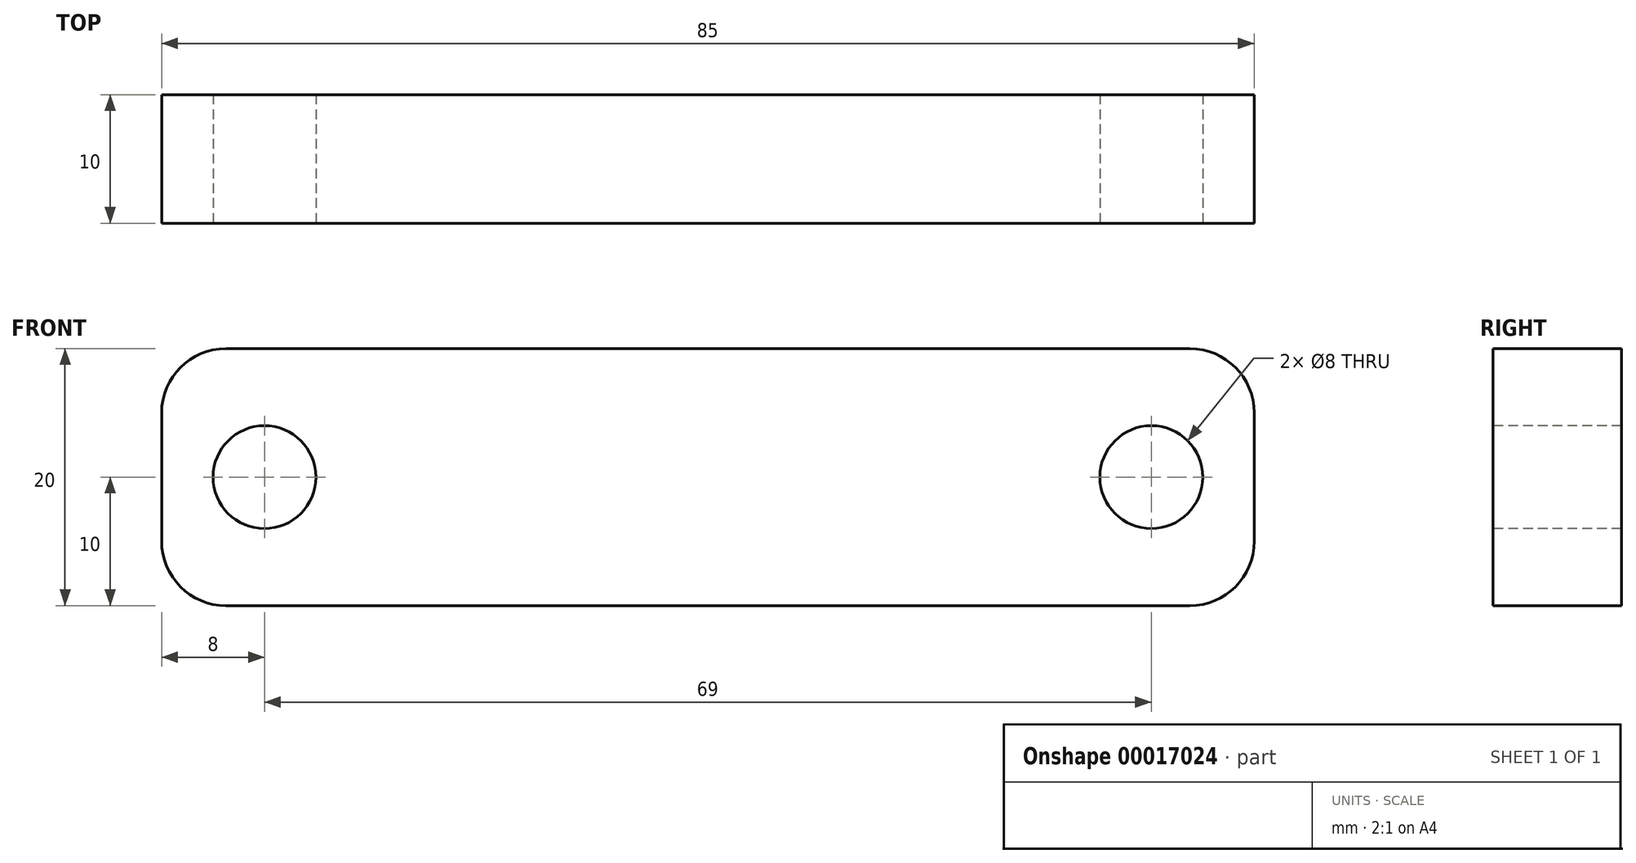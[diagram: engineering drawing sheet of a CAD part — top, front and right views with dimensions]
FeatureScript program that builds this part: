
annotation { "Feature Type Name" : "Feature", "Feature Type Description" : "" }
export const myFeature = defineFeature(function(context is Context, id is Id, definition is map)
    precondition{}
    {
        {
            var Q0;
            Q0=qCreatedBy(makeId("Front.planeOp"),FACE);
            var sketch = newSketch(context, id + "F0", { "sketchPlane" : qUnion([Q0])});
            skLineSegment(sketch, "E0.bottom", {"start": v(-40, 10) * mm, "end": v(45, 10) * mm});
            skLineSegment(sketch, "E0.top", {"start": v(-40, -10) * mm, "end": v(45, -10) * mm});
            skLineSegment(sketch, "E0.left", {"start": v(-40, 10) * mm, "end": v(-40, -10) * mm});
            skLineSegment(sketch, "E0.right", {"start": v(45, 10) * mm, "end": v(45, -10) * mm});
            skSolve(sketch);
        }
        {
            var Q0;
            Q0 = qSketchRegion(id + "F0", true);
            extrude(context, id + "F1", {"entities" : qUnion([Q0]), "depth" : 10 * mm});
        }
        {
            var Q0;
            Q0=makeQuery(id+"F1.opExtrude","CAP_FACE",FACE,{"disambiguationData":[OSD([sQuery(id+"F0.wireOp",EDGE,"E0.bottom"),sQuery(id+"F0.wireOp",EDGE,"E0.top"),sQuery(id+"F0.wireOp",EDGE,"E0.left"),sQuery(id+"F0.wireOp",EDGE,"E0.right")])],"isStart":false});
            var sketch = newSketch(context, id + "F2", { "sketchPlane" : qUnion([Q0])});
            skCircle(sketch, "E1", {"center": v(37, 0) * mm, "radius": 4 * mm});
            skCircle(sketch, "E2", {"center": v(-32, 0) * mm, "radius": 4 * mm});
            skSolve(sketch);
        }
        {
            var Q0;
            Q0 = qSketchRegion(id + "F2", true);
            extrude(context, id + "F3", {"entities" : qUnion([Q0]), "operationType" : NewBodyOperationType.REMOVE, "endBound" : BoundingType.THROUGH_ALL, "oppositeDirection" : true, "depth" : 25 * mm});
        }
        {
            var Q0;
            Q0=makeQuery(id+"F1.opExtrude","SWEPT_EDGE",EDGE,{"disambiguationData":[OSD([sQuery(id+"F0.wireOp",EDGE,"E0.top"),sQuery(id+"F0.wireOp",EDGE,"E0.left")])]});
            var Q1;
            Q1=makeQuery(id+"F1.opExtrude","SWEPT_EDGE",EDGE,{"disambiguationData":[OSD([sQuery(id+"F0.wireOp",EDGE,"E0.top"),sQuery(id+"F0.wireOp",EDGE,"E0.right")])]});
            var Q2;
            Q2=makeQuery(id+"F1.opExtrude","SWEPT_EDGE",EDGE,{"disambiguationData":[OSD([sQuery(id+"F0.wireOp",EDGE,"E0.bottom"),sQuery(id+"F0.wireOp",EDGE,"E0.right")])]});
            var Q3;
            Q3=makeQuery(id+"F1.opExtrude","SWEPT_EDGE",EDGE,{"disambiguationData":[OSD([sQuery(id+"F0.wireOp",EDGE,"E0.bottom"),sQuery(id+"F0.wireOp",EDGE,"E0.left")])]});
            fillet(context, id + "F4", {"entities" : qUnion([Q0, Q1, Q2, Q3]), "radius" : 5 * mm, "tangentPropagation" : true, "allowEdgeOverflow" : false});
        }
    });
